# Revit family: Furniture-Vanity_Legs-KOHLER-SEER-K-32813_1
name_source: partatom
category: Specialty Equipment
revit_build: Autodesk Revit 2017 (Build: 20160225_1515(x64)
units: mm (PartAtom-declared; Revit-internal decimal feet)

## family parameters
Cut with Voids When Loaded = No
Host = Face
OmniClass Number = 23.31.25.00
OmniClass Title = Toilet and Bath Specialties
Part Type = Normal
Room Calculation Point = No
Round Connector Dimension = Use Diameter
Shared = No

## types (1)
- 1WD-Ramie Walnut
    ADA Compliant = No
    Assembly Code = C1030200
    Date Modified = 02/15/2021
    Default Elevation = 0"
    Description = LEGS 24 INCHES
    Finish = Kohler-Wood-1WD-Ramie_Walnut
    Height = 8 9/16"
    Length = 17 5/16"
    Manufacturer = KOHLER Co.
    Master Format 2014 = 10 28 00
    Master Format 2014 Name = Toilet, Bath, and Laundry Accessories
    Material = Solid Wood
    Model = K-32813-SH1-1WD
    Product Name = SEER
    Type = 1
    URL = https://www.us.kohler.com
    WaterSense Certified = No
    Width = 24"

## geometry (parser evidence)
native form markers: Sweep x5
no freeform markers — native parametric forms only
